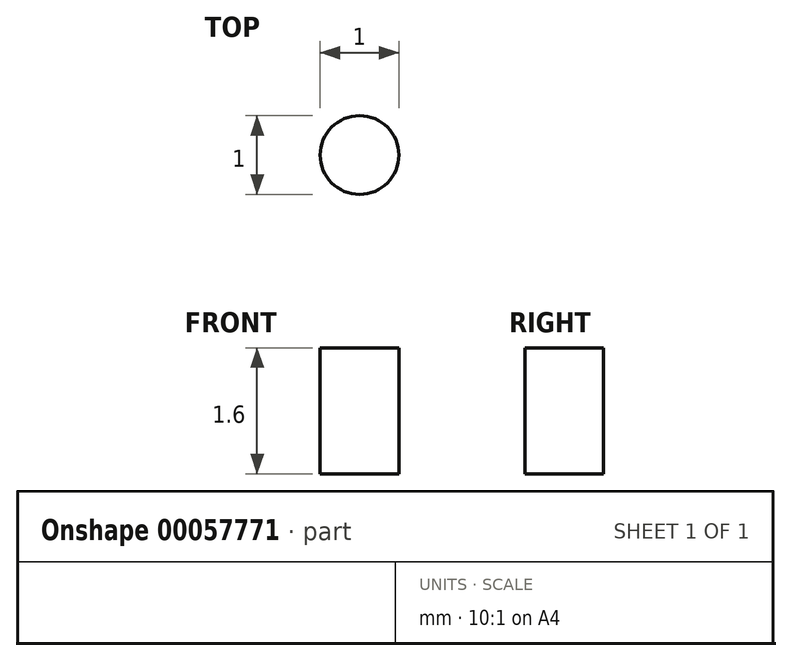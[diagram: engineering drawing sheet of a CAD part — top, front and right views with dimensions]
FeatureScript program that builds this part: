
annotation { "Feature Type Name" : "Feature", "Feature Type Description" : "" }
export const myFeature = defineFeature(function(context is Context, id is Id, definition is map)
    precondition{}
    {
        {
            var Q0;
            Q0=qCreatedBy(makeId("Top.planeOp"),FACE);
            var sketch = newSketch(context, id + "F0", { "sketchPlane" : qUnion([Q0])});
            skCircle(sketch, "E0", {"center": v(0, 0) * mm, "radius": 94 * mm});
            skSolve(sketch);
        }
        {
            var Q0;
            Q0 = qSketchRegion(id + "F0", true);
            extrude(context, id + "F1", {"entities" : qUnion([Q0]), "depth" : 1.6 * mm});
        }
        {
            var Q0;
            Q0=qCreatedBy(makeId("Top.planeOp"),FACE);
            var sketch = newSketch(context, id + "F2", { "sketchPlane" : qUnion([Q0])});
            skCircle(sketch, "E1", {"center": v(0, 62.5) * mm, "radius": 0.6 * mm});
            skCircle(sketch, "E2.1.0", {"center": v(-31.25, 54.13) * mm, "radius": 0.6 * mm});
            skCircle(sketch, "E2.2.0", {"center": v(-54.13, 31.25) * mm, "radius": 0.6 * mm});
            skCircle(sketch, "E2.3.0", {"center": v(-62.5, 0) * mm, "radius": 0.6 * mm});
            skCircle(sketch, "E2.4.0", {"center": v(-54.13, -31.25) * mm, "radius": 0.6 * mm});
            skCircle(sketch, "E2.5.0", {"center": v(-31.25, -54.13) * mm, "radius": 0.6 * mm});
            skCircle(sketch, "E2.6.0", {"center": v(0, -62.5) * mm, "radius": 0.6 * mm});
            skCircle(sketch, "E2.7.0", {"center": v(31.25, -54.13) * mm, "radius": 0.6 * mm});
            skCircle(sketch, "E2.8.0", {"center": v(54.13, -31.25) * mm, "radius": 0.6 * mm});
            skCircle(sketch, "E2.9.0", {"center": v(62.5, 0) * mm, "radius": 0.6 * mm});
            skCircle(sketch, "E2.10.0", {"center": v(54.13, 31.25) * mm, "radius": 0.6 * mm});
            skCircle(sketch, "E2.11.0", {"center": v(31.25, 54.13) * mm, "radius": 0.6 * mm});
            skPoint(sketch, "E2.center", {"position": v(0, 0) * mm});
            skSolve(sketch);
        }
        {
            var Q0;
            Q0 = qSketchRegion(id + "F2", true);
            var Q1;
            Q1=makeQuery(id+"F1.opExtrude","SWEPT_BODY",BODY,{"disambiguationData":[OSD([sQuery(id+"F0.wireOp",EDGE,"E0")])]});
            extrude(context, id + "F3", {"entities" : qUnion([Q0]), "operationType" : NewBodyOperationType.REMOVE, "endBound" : BoundingType.UP_TO_BODY, "endBoundEntityBody" : qUnion([Q1]), "depth" : 25 * mm});
        }
        {
            var Q0;
            Q0=makeQuery(id+"F1.opExtrude","CAP_FACE",FACE,{"disambiguationData":[OSD([sQuery(id+"F0.wireOp",EDGE,"E0")])],"isStart":false});
            var sketch = newSketch(context, id + "F4", { "sketchPlane" : qUnion([Q0])});
            skCircle(sketch, "E3", {"center": v(0, 0) * mm, "radius": 72 * mm, "construction": true});
            skCircle(sketch, "E4", {"center": v(0, 0) * mm, "radius": 79 * mm, "construction": true});
            skLineSegment(sketch, "E5.0", {"start": v(-4.5, 79.5) * mm, "end": v(4.5, 79.5) * mm});
            skCircle(sketch, "E6.0", {"center": v(0, 0) * mm, "radius": 99 * mm});
            skLineSegment(sketch, "E7.0", {"start": v(-4.5, 71.5) * mm, "end": v(4.5, 71.5) * mm});
            skLineSegment(sketch, "E8.0", {"start": v(-6, 78) * mm, "end": v(-6, 73) * mm});
            skLineSegment(sketch, "E9.0", {"start": v(6, 78) * mm, "end": v(6, 73) * mm});
            skPoint(sketch, "E10.visualSharp", {"position": v(-6, 79.5) * mm});
            skArc(sketch, "E10.filletArc", {"start": v(-4.5, 79.5) * mm, "mid": v(-5.56, 79.06) * mm, "end": v(-6, 78) * mm});
            skPoint(sketch, "E11.visualSharp", {"position": v(6, 79.5) * mm});
            skArc(sketch, "E11.filletArc", {"start": v(6, 78) * mm, "mid": v(5.56, 79.06) * mm, "end": v(4.5, 79.5) * mm});
            skPoint(sketch, "E12.visualSharp", {"position": v(6, 71.5) * mm});
            skArc(sketch, "E12.filletArc", {"start": v(4.5, 71.5) * mm, "mid": v(5.56, 71.94) * mm, "end": v(6, 73) * mm});
            skPoint(sketch, "E13.visualSharp", {"position": v(-6, 71.5) * mm});
            skArc(sketch, "E13.filletArc", {"start": v(-6, 73) * mm, "mid": v(-5.56, 71.94) * mm, "end": v(-4.5, 71.5) * mm});
            skSolve(sketch);
        }
        {
            var Q0;
            Q0=makeQuery(id+"F4.imprint","IMPRINT",FACE,{"disambiguationData":[TD([[makeQuery(id+"F4.imprint","IMPRINT",EDGE,{"derivedFrom":sQuery(id+"F4.wireOp",EDGE,"E5.0")}),-1.0]])]});
            var Q1;
            Q1=makeQuery(id+"F1.opExtrude","SWEPT_BODY",BODY,{"disambiguationData":[OSD([sQuery(id+"F0.wireOp",EDGE,"E0")])]});
            extrude(context, id + "F5", {"entities" : qUnion([Q0]), "operationType" : NewBodyOperationType.REMOVE, "endBound" : BoundingType.UP_TO_BODY, "oppositeDirection" : true, "endBoundEntityBody" : qUnion([Q1]), "depth" : 25 * mm});
        }
        {
            var Q0;
            Q0=makeQuery(id+"F5.boolean.opBoolean","COPY",FACE,{"derivedFrom":makeQuery(id+"F5.opExtrude","SWEPT_FACE",FACE,{"disambiguationData":[OSD([sQuery(id+"F4.wireOp",EDGE,"E8.0")])]})});
            var Q1;
            Q1=makeQuery(id+"F5.boolean.opBoolean","COPY",FACE,{"derivedFrom":makeQuery(id+"F5.opExtrude","SWEPT_FACE",FACE,{"disambiguationData":[OSD([sQuery(id+"F4.wireOp",EDGE,"E10.filletArc")])]})});
            var Q2;
            Q2=makeQuery(id+"F5.boolean.opBoolean","COPY",FACE,{"derivedFrom":makeQuery(id+"F5.opExtrude","SWEPT_FACE",FACE,{"disambiguationData":[OSD([sQuery(id+"F4.wireOp",EDGE,"E13.filletArc")])]})});
            var Q3;
            Q3=makeQuery(id+"F5.boolean.opBoolean","COPY",FACE,{"derivedFrom":makeQuery(id+"F5.opExtrude","SWEPT_FACE",FACE,{"disambiguationData":[OSD([sQuery(id+"F4.wireOp",EDGE,"E5.0")])]})});
            var Q4;
            Q4=makeQuery(id+"F5.boolean.opBoolean","COPY",FACE,{"derivedFrom":makeQuery(id+"F5.opExtrude","SWEPT_FACE",FACE,{"disambiguationData":[OSD([sQuery(id+"F4.wireOp",EDGE,"E11.filletArc")])]})});
            var Q5;
            Q5=makeQuery(id+"F5.boolean.opBoolean","COPY",FACE,{"derivedFrom":makeQuery(id+"F5.opExtrude","SWEPT_FACE",FACE,{"disambiguationData":[OSD([sQuery(id+"F4.wireOp",EDGE,"E9.0")])]})});
            var Q6;
            Q6=makeQuery(id+"F5.boolean.opBoolean","COPY",FACE,{"derivedFrom":makeQuery(id+"F5.opExtrude","SWEPT_FACE",FACE,{"disambiguationData":[OSD([sQuery(id+"F4.wireOp",EDGE,"E12.filletArc")])]})});
            var Q7;
            Q7=makeQuery(id+"F5.boolean.opBoolean","COPY",FACE,{"derivedFrom":makeQuery(id+"F5.opExtrude","SWEPT_FACE",FACE,{"disambiguationData":[OSD([sQuery(id+"F4.wireOp",EDGE,"E7.0")])]})});
            var Q8;
            Q8=makeQuery(id+"F1.opExtrude","CAP_EDGE",EDGE,{"disambiguationData":[OSD([sQuery(id+"F0.wireOp",EDGE,"E0")])],"isStart":false});
            circularPattern(context, id + "F6", {"faces" : qUnion([Q0, Q1, Q2, Q3, Q4, Q5, Q6, Q7]), "axis" : qUnion([Q8]), "angle" : 45 * degree, "instanceCount" : 8, "patternType" : PatternType.FACE});
        }
        {
            var Q0;
            Q0=makeQuery(id+"F1.opExtrude","CAP_FACE",FACE,{"disambiguationData":[OSD([sQuery(id+"F0.wireOp",EDGE,"E0")])],"isStart":true});
            var sketch = newSketch(context, id + "F7", { "sketchPlane" : qUnion([Q0])});
            skLineSegment(sketch, "E14.bottom", {"start": v(-19.9, 43.4) * mm, "end": v(-0.9, 43.4) * mm});
            skLineSegment(sketch, "E14.top", {"start": v(-19.9, 34.9) * mm, "end": v(-0.9, 34.9) * mm});
            skLineSegment(sketch, "E14.left", {"start": v(-21.4, 41.9) * mm, "end": v(-21.4, 36.4) * mm});
            skLineSegment(sketch, "E14.right", {"start": v(0.6, 41.9) * mm, "end": v(0.6, 36.4) * mm});
            skPoint(sketch, "E15.visualSharp", {"position": v(-21.4, 43.4) * mm});
            skArc(sketch, "E15.filletArc", {"start": v(-19.9, 43.4) * mm, "mid": v(-20.96, 42.96) * mm, "end": v(-21.4, 41.9) * mm});
            skPoint(sketch, "E16.visualSharp", {"position": v(0.6, 43.4) * mm});
            skArc(sketch, "E16.filletArc", {"start": v(0.6, 41.9) * mm, "mid": v(0.16, 42.96) * mm, "end": v(-0.9, 43.4) * mm});
            skPoint(sketch, "E17.visualSharp", {"position": v(0.6, 34.9) * mm});
            skArc(sketch, "E17.filletArc", {"start": v(-0.9, 34.9) * mm, "mid": v(0.16, 35.34) * mm, "end": v(0.6, 36.4) * mm});
            skPoint(sketch, "E18.visualSharp", {"position": v(-21.4, 34.9) * mm});
            skArc(sketch, "E18.filletArc", {"start": v(-21.4, 36.4) * mm, "mid": v(-20.96, 35.34) * mm, "end": v(-19.9, 34.9) * mm});
            skSolve(sketch);
        }
        {
            var Q0;
            Q0 = qSketchRegion(id + "F7", true);
            var Q1;
            Q1=makeQuery(id+"F1.opExtrude","SWEPT_BODY",BODY,{"disambiguationData":[OSD([sQuery(id+"F0.wireOp",EDGE,"E0")])]});
            extrude(context, id + "F8", {"entities" : qUnion([Q0]), "operationType" : NewBodyOperationType.REMOVE, "endBound" : BoundingType.UP_TO_BODY, "oppositeDirection" : true, "endBoundEntityBody" : qUnion([Q1]), "depth" : 25 * mm});
        }
        {
            var Q0;
            Q0=makeQuery(id+"F1.opExtrude","CAP_FACE",FACE,{"disambiguationData":[OSD([sQuery(id+"F0.wireOp",EDGE,"E0")])],"isStart":false});
            var sketch = newSketch(context, id + "F9", { "sketchPlane" : qUnion([Q0])});
            skCircle(sketch, "E19", {"center": v(-2, 20) * mm, "radius": 0.5 * mm});
            skCircle(sketch, "E20.MirrorC", {"center": v(2, 20) * mm, "radius": 0.5 * mm});
            skCircle(sketch, "E21", {"center": v(0, 0) * mm, "radius": 5 * mm});
            skSolve(sketch);
        }
        {
            var Q0;
            Q0=makeQuery(id+"F9.imprint","IMPRINT",FACE,{"disambiguationData":[TD([[makeQuery(id+"F9.imprint","IMPRINT",EDGE,{"derivedFrom":sQuery(id+"F9.wireOp",EDGE,"E19")}),1.0]])]});
            var Q1;
            Q1=makeQuery(id+"F9.imprint","IMPRINT",FACE,{"disambiguationData":[TD([[makeQuery(id+"F9.imprint","IMPRINT",EDGE,{"derivedFrom":sQuery(id+"F9.wireOp",EDGE,"E20.MirrorC")}),-1.0]])]});
            var Q2;
            Q2=makeQuery(id+"F9.imprint","IMPRINT",FACE,{"disambiguationData":[TD([[makeQuery(id+"F9.imprint","IMPRINT",EDGE,{"derivedFrom":sQuery(id+"F9.wireOp",EDGE,"E21")}),1.0]])]});
            var Q3;
            Q3=makeQuery(id+"F1.opExtrude","SWEPT_BODY",BODY,{"disambiguationData":[OSD([sQuery(id+"F0.wireOp",EDGE,"E0")])]});
            extrude(context, id + "F10", {"entities" : qUnion([Q0, Q1, Q2]), "operationType" : NewBodyOperationType.REMOVE, "endBound" : BoundingType.UP_TO_BODY, "oppositeDirection" : true, "endBoundEntityBody" : qUnion([Q3]), "depth" : 25 * mm});
        }
    });
